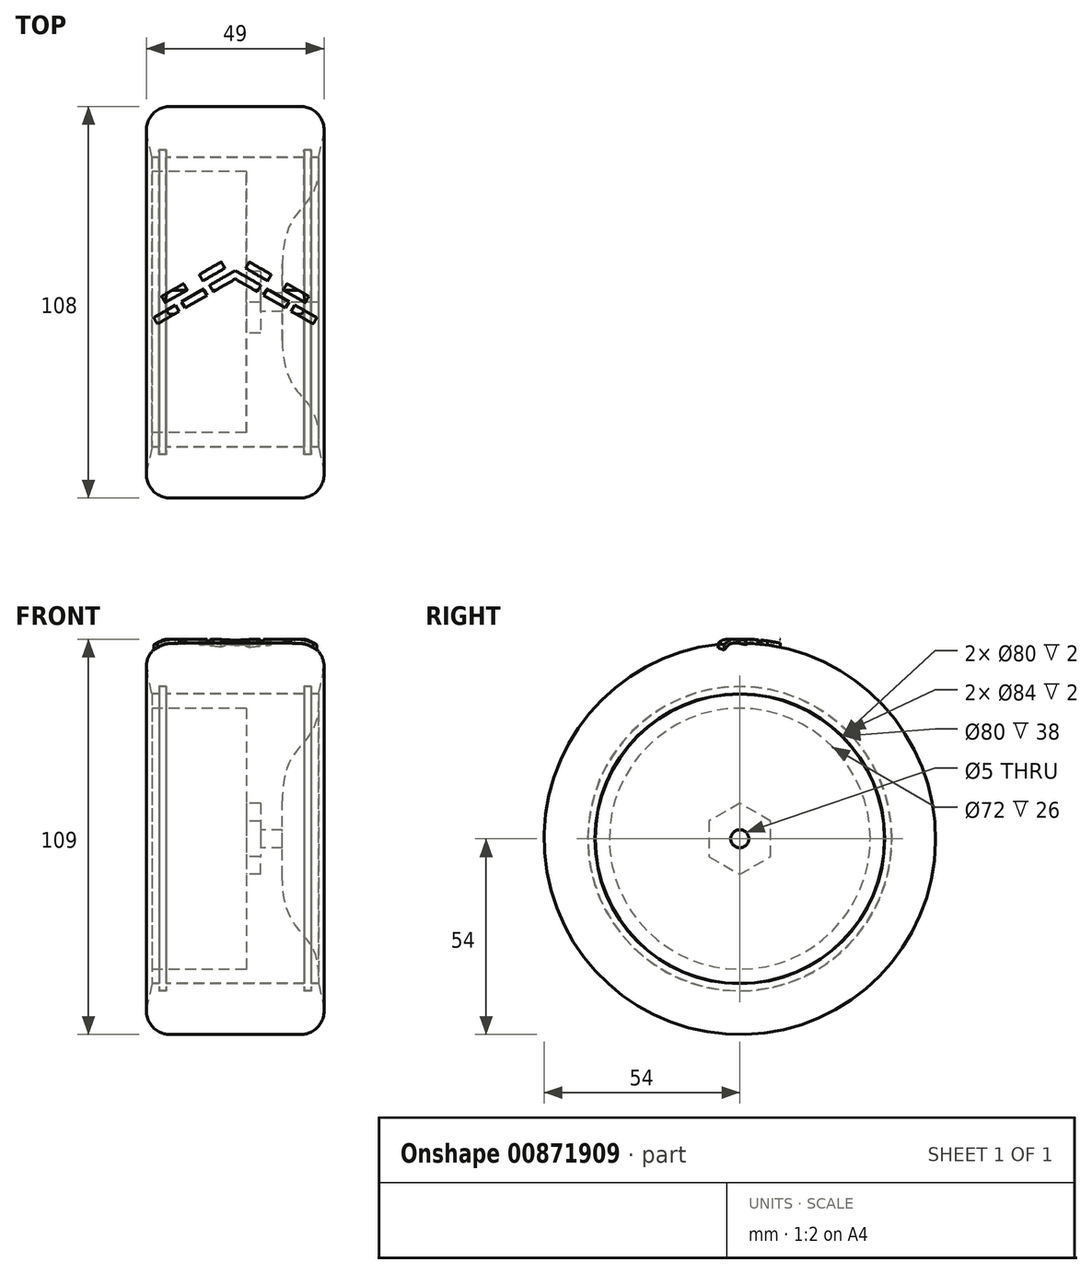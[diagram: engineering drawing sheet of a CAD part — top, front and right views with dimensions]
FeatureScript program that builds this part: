
annotation { "Feature Type Name" : "Feature", "Feature Type Description" : "" }
export const myFeature = defineFeature(function(context is Context, id is Id, definition is map)
    precondition{}
    {
        {
            var Q0;
            Q0=qCreatedBy(makeId("Front.planeOp"),FACE);
            var sketch = newSketch(context, id + "F0", { "sketchPlane" : qUnion([Q0])});
            skLineSegment(sketch, "E0", {"start": v(0, 0) * mm, "end": v(28.5, 0) * mm, "construction": true});
            skLineSegment(sketch, "E1", {"start": v(23, 2.5) * mm, "end": v(3, 2.5) * mm});
            skLineSegment(sketch, "E2", {"start": v(3, 2.5) * mm, "end": v(3, 36) * mm});
            skLineSegment(sketch, "E3", {"start": v(3, 36) * mm, "end": v(-23, 36) * mm});
            skLineSegment(sketch, "E4", {"start": v(-23, 36) * mm, "end": v(-23, 39.9) * mm});
            skLineSegment(sketch, "E5", {"start": v(-15, 54) * mm, "end": v(18, 54) * mm, "construction": true});
            skLineSegment(sketch, "E6", {"start": v(23, 46) * mm, "end": v(23, 40) * mm, "construction": true});
            skLineSegment(sketch, "E7", {"start": v(-23, 40) * mm, "end": v(-21, 40) * mm});
            skLineSegment(sketch, "E8", {"start": v(-21, 40) * mm, "end": v(-21, 42) * mm});
            skLineSegment(sketch, "E9", {"start": v(-21, 42) * mm, "end": v(-19, 42) * mm});
            skLineSegment(sketch, "E10", {"start": v(-19, 42) * mm, "end": v(-19, 40) * mm});
            skLineSegment(sketch, "E11", {"start": v(-19, 40) * mm, "end": v(19, 40) * mm});
            skLineSegment(sketch, "E12", {"start": v(19, 40) * mm, "end": v(19, 42) * mm});
            skLineSegment(sketch, "E13", {"start": v(19, 42) * mm, "end": v(21, 42) * mm});
            skLineSegment(sketch, "E14", {"start": v(21, 42) * mm, "end": v(21, 40) * mm});
            skLineSegment(sketch, "E15", {"start": v(21, 40) * mm, "end": v(23, 40) * mm});
            skLineSegment(sketch, "E16.0", {"start": v(20.9, 39.9) * mm, "end": v(23, 39.9) * mm});
            skLineSegment(sketch, "E16.1", {"start": v(20.9, 41.9) * mm, "end": v(20.9, 39.9) * mm});
            skLineSegment(sketch, "E16.2", {"start": v(19.1, 41.9) * mm, "end": v(20.9, 41.9) * mm});
            skLineSegment(sketch, "E16.3", {"start": v(19.1, 39.9) * mm, "end": v(19.1, 41.9) * mm});
            skLineSegment(sketch, "E16.4", {"start": v(-19.1, 39.9) * mm, "end": v(19.1, 39.9) * mm});
            skLineSegment(sketch, "E16.5", {"start": v(-23, 39.9) * mm, "end": v(-20.9, 39.9) * mm});
            skLineSegment(sketch, "E16.6", {"start": v(-20.9, 39.9) * mm, "end": v(-20.9, 41.9) * mm});
            skLineSegment(sketch, "E16.7", {"start": v(-20.9, 41.9) * mm, "end": v(-19.1, 41.9) * mm});
            skLineSegment(sketch, "E16.8", {"start": v(-19.1, 41.9) * mm, "end": v(-19.1, 39.9) * mm});
            skLineSegment(sketch, "E17.trimOffspring", {"start": v(-23, 40) * mm, "end": v(-23, 46) * mm, "construction": true});
            skLineSegment(sketch, "E18.trimOffspring", {"start": v(23, 39.9) * mm, "end": v(23, 2.5) * mm});
            skPoint(sketch, "E19.visualSharp", {"position": v(-23, 54) * mm});
            skArc(sketch, "E19.filletArc", {"start": v(-15, 54) * mm, "mid": v(-20.66, 51.66) * mm, "end": v(-23, 46) * mm, "construction": true});
            skPoint(sketch, "E20.visualSharp", {"position": v(23, 54) * mm});
            skArc(sketch, "E20.filletArc", {"start": v(23, 46) * mm, "mid": v(20.66, 51.66) * mm, "end": v(15, 54) * mm, "construction": true});
            skLineSegment(sketch, "E21", {"start": v(23, 40) * mm, "end": v(24.35, 46.1) * mm});
            skArc(sketch, "E22", {"start": v(24.35, 46.1) * mm, "mid": v(23.07, 51.57) * mm, "end": v(18, 54) * mm});
            skLineSegment(sketch, "E23", {"start": v(0, 40) * mm, "end": v(0, 59.6) * mm, "construction": true});
            skArc(sketch, "E24.MirrorCS", {"start": v(-24.35, 46.1) * mm, "mid": v(-23.07, 51.57) * mm, "end": v(-18, 54) * mm});
            skLineSegment(sketch, "E25.MirrorCS", {"start": v(-23, 40) * mm, "end": v(-24.35, 46.1) * mm});
            skLineSegment(sketch, "E26", {"start": v(-18, 54) * mm, "end": v(18, 54) * mm});
            skSolve(sketch);
        }
        {
            var Q0;
            Q0=qSketchRegion(id+"F0",true);
            var Q1;
            Q1=sQuery(id+"F0.wireOp",EDGE,"E0");
            revolve(context, id + "F1", {"surfaceOperationType" : NewSurfaceOperationType.NEW, "entities" : qUnion([Q0]), "axis" : qUnion([Q1]), "revolveType" : RevolveType.FULL});
        }
        {
            var Q0;
            Q0=makeQuery(id+"F1.opRevolve","SWEPT_FACE",FACE,{"disambiguationData":[OSD([sQuery(id+"F0.wireOp",EDGE,"E2")])]});
            var sketch = newSketch(context, id + "F2", { "sketchPlane" : qUnion([Q0])});
            skCircle(sketch, "E27.cCircle", {"center": v(0, 0) * mm, "radius": 9.81 * mm, "construction": true});
            skLineSegment(sketch, "E27.0", {"start": v(8.5, 4.9) * mm, "end": v(8.5, -4.9) * mm});
            skLineSegment(sketch, "E27.1", {"start": v(8.5, -4.9) * mm, "end": v(0, -9.81) * mm});
            skLineSegment(sketch, "E27.2", {"start": v(0, -9.81) * mm, "end": v(-8.5, -4.9) * mm});
            skLineSegment(sketch, "E27.3", {"start": v(-8.5, -4.9) * mm, "end": v(-8.5, 4.9) * mm});
            skLineSegment(sketch, "E27.4", {"start": v(-8.5, 4.9) * mm, "end": v(0, 9.81) * mm});
            skLineSegment(sketch, "E27.5", {"start": v(0, 9.81) * mm, "end": v(8.5, 4.9) * mm});
            skSolve(sketch);
        }
        {
            var Q0;
            Q0=qSketchRegion(id+"F2",true);
            extrude(context, id + "F3", {"entities" : qUnion([Q0]), "operationType" : NewBodyOperationType.REMOVE, "oppositeDirection" : true, "depth" : 4 * mm, "offsetDistance" : 25 * mm});
        }
        {
            var Q0;
            Q0=qCreatedBy(makeId("Front.planeOp"),FACE);
            var sketch = newSketch(context, id + "F4", { "sketchPlane" : qUnion([Q0])});
            skLineSegment(sketch, "E28", {"start": v(0, 0) * mm, "end": v(45.35, 0) * mm, "construction": true});
            skLineSegment(sketch, "E29", {"start": v(13, 0) * mm, "end": v(13, 10.5) * mm});
            skLineSegment(sketch, "E30", {"start": v(20.9, 39.9) * mm, "end": v(23, 39.9) * mm, "construction": true});
            skLineSegment(sketch, "E31", {"start": v(23, 39.9) * mm, "end": v(23, 37.9) * mm});
            skFitSpline(sketch, "E32", {"points": [v(23, 37.9) * mm, v(13, 10.5) * mm], "startDerivative": vector(0, -41.43) * mm, "endDerivative": vector(0, -52.48) * mm});
            skLineSegment(sketch, "E33", {"start": v(23, 39.9) * mm, "end": v(24, 39.9) * mm});
            skLineSegment(sketch, "E34", {"start": v(24, 39.9) * mm, "end": v(24, 0) * mm});
            skLineSegment(sketch, "E35", {"start": v(24, 0) * mm, "end": v(13, 0) * mm});
            skSolve(sketch);
        }
        {
            var Q0;
            Q0=makeQuery(id+"F4.imprint","IMPRINT",FACE,{"disambiguationData":[TD([[makeQuery(id+"F4.imprint","IMPRINT",EDGE,{"derivedFrom":sQuery(id+"F4.wireOp",EDGE,"E29")}),-1.0]])]});
            var Q1;
            Q1=sQuery(id+"F4.wireOp",EDGE,"E28");
            revolve(context, id + "F5", {"operationType" : NewBodyOperationType.REMOVE, "surfaceOperationType" : NewSurfaceOperationType.NEW, "entities" : qUnion([Q0]), "axis" : qUnion([Q1]), "revolveType" : RevolveType.FULL, "oppositeDirection" : true});
        }
        {
            var Q0;
            Q0=qCreatedBy(makeId("Top.planeOp"),FACE);
            cPlane(context, id + "F6", {"entities" : qUnion([Q0]), "cplaneType" : CPlaneType.OFFSET, "offset" : (110 / 2) * mm, "width" : 150 * mm, "height" : 150 * mm});
        }
        {
            var Q0;
            Q0=qCreatedBy(id+"F6.planeOp",FACE);
            var sketch = newSketch(context, id + "F7", { "sketchPlane" : qUnion([Q0])});
            skLineSegment(sketch, "E36", {"start": v(-24.5, -48.5) * mm, "end": v(-24.5, 48.5) * mm, "construction": true});
            skLineSegment(sketch, "E37", {"start": v(24.5, -48.5) * mm, "end": v(24.5, 48.5) * mm, "construction": true});
            skLineSegment(sketch, "E38", {"start": v(-24.5, 0) * mm, "end": v(24.5, 0) * mm, "construction": true});
            skLineSegment(sketch, "E39", {"start": v(-21.5, -6) * mm, "end": v(0, 6.41) * mm, "construction": true});
            skLineSegment(sketch, "E40", {"start": v(0, 6.41) * mm, "end": v(21.5, -6) * mm, "construction": true});
            skLineSegment(sketch, "E41", {"start": v(21.5, -6) * mm, "end": v(22.5, -4.27) * mm});
            skLineSegment(sketch, "E42", {"start": v(22.5, -4.27) * mm, "end": v(0, 8.72) * mm, "construction": true});
            skLineSegment(sketch, "E43", {"start": v(0, 8.72) * mm, "end": v(-22.5, -4.27) * mm, "construction": true});
            skLineSegment(sketch, "E44", {"start": v(-22.5, -4.27) * mm, "end": v(-21.5, -6) * mm});
            skLineSegment(sketch, "E45", {"start": v(0, 0) * mm, "end": v(0, 13.9) * mm, "construction": true});
            skLineSegment(sketch, "E46", {"start": v(-21.5, -6) * mm, "end": v(21.5, -6) * mm, "construction": true});
            skLineSegment(sketch, "E47", {"start": v(0, 0) * mm, "end": v(0, -10.86) * mm, "construction": true});
            skLineSegment(sketch, "E48", {"start": v(21.5, -6) * mm, "end": v(15.44, -2.5) * mm});
            skLineSegment(sketch, "E49", {"start": v(15.44, -2.5) * mm, "end": v(16.44, -0.77) * mm});
            skLineSegment(sketch, "E50", {"start": v(16.44, -0.77) * mm, "end": v(22.5, -4.27) * mm});
            skLineSegment(sketch, "E51", {"start": v(-21.5, -6) * mm, "end": v(-15.44, -2.5) * mm});
            skLineSegment(sketch, "E52", {"start": v(-15.44, -2.5) * mm, "end": v(-16.44, -0.77) * mm});
            skLineSegment(sketch, "E53", {"start": v(-16.44, -0.77) * mm, "end": v(-22.5, -4.27) * mm});
            skLineSegment(sketch, "E54", {"start": v(-14.86, 0.15) * mm, "end": v(-13.86, -1.59) * mm});
            skLineSegment(sketch, "E55", {"start": v(-13.86, -1.59) * mm, "end": v(-7.8, 1.91) * mm});
            skLineSegment(sketch, "E56", {"start": v(-7.8, 1.91) * mm, "end": v(-8.8, 3.65) * mm});
            skLineSegment(sketch, "E57", {"start": v(-8.8, 3.65) * mm, "end": v(-14.86, 0.15) * mm});
            skLineSegment(sketch, "E58", {"start": v(8.8, 3.65) * mm, "end": v(7.8, 1.91) * mm});
            skLineSegment(sketch, "E59", {"start": v(7.8, 1.91) * mm, "end": v(13.86, -1.59) * mm});
            skLineSegment(sketch, "E60", {"start": v(13.86, -1.59) * mm, "end": v(14.86, 0.15) * mm});
            skLineSegment(sketch, "E61", {"start": v(14.86, 0.15) * mm, "end": v(8.8, 3.65) * mm});
            skLineSegment(sketch, "E62", {"start": v(7.06, 4.65) * mm, "end": v(6.06, 2.91) * mm});
            skLineSegment(sketch, "E63", {"start": v(6.06, 2.91) * mm, "end": v(0, 6.41) * mm});
            skLineSegment(sketch, "E64", {"start": v(-6.06, 2.91) * mm, "end": v(-7.06, 4.65) * mm});
            skLineSegment(sketch, "E65", {"start": v(-7.06, 4.65) * mm, "end": v(0, 8.72) * mm});
            skLineSegment(sketch, "E66", {"start": v(7.06, 4.65) * mm, "end": v(0, 8.72) * mm});
            skLineSegment(sketch, "E67", {"start": v(-6.06, 2.91) * mm, "end": v(0, 6.41) * mm});
            skLineSegment(sketch, "E68.0", {"start": v(0, 11.03) * mm, "end": v(-23.5, -2.54) * mm, "construction": true});
            skLineSegment(sketch, "E68.1", {"start": v(23.5, -2.54) * mm, "end": v(0, 11.03) * mm, "construction": true});
            skLineSegment(sketch, "E69.0", {"start": v(-1, 12.76) * mm, "end": v(-24.5, -0.8) * mm, "construction": true});
            skLineSegment(sketch, "E70", {"start": v(-20.32, 1.6) * mm, "end": v(-19.32, -0.12) * mm});
            skLineSegment(sketch, "E71", {"start": v(-19.32, -0.12) * mm, "end": v(-13.26, 3.38) * mm});
            skLineSegment(sketch, "E72", {"start": v(-13.26, 3.38) * mm, "end": v(-14.26, 5.1) * mm});
            skLineSegment(sketch, "E73", {"start": v(-14.26, 5.1) * mm, "end": v(-20.32, 1.6) * mm});
            skLineSegment(sketch, "E74", {"start": v(-8.93, 5.88) * mm, "end": v(-9.93, 7.6) * mm});
            skLineSegment(sketch, "E75", {"start": v(-9.93, 7.6) * mm, "end": v(-3.87, 11.1) * mm});
            skLineSegment(sketch, "E76", {"start": v(-3.87, 11.1) * mm, "end": v(-2.87, 9.38) * mm});
            skLineSegment(sketch, "E77", {"start": v(-2.87, 9.38) * mm, "end": v(-8.93, 5.88) * mm});
            skLineSegment(sketch, "E78.MirrorCS", {"start": v(3.87, 11.1) * mm, "end": v(2.87, 9.38) * mm});
            skLineSegment(sketch, "E79.MirrorCS", {"start": v(8.93, 5.88) * mm, "end": v(9.93, 7.6) * mm});
            skLineSegment(sketch, "E80.MirrorCS", {"start": v(13.26, 3.38) * mm, "end": v(14.26, 5.1) * mm});
            skLineSegment(sketch, "E81.MirrorCS", {"start": v(20.32, 1.6) * mm, "end": v(19.32, -0.12) * mm});
            skLineSegment(sketch, "E82", {"start": v(2.87, 9.38) * mm, "end": v(8.93, 5.88) * mm});
            skLineSegment(sketch, "E83", {"start": v(9.93, 7.6) * mm, "end": v(3.87, 11.1) * mm});
            skLineSegment(sketch, "E84", {"start": v(14.26, 5.1) * mm, "end": v(20.32, 1.6) * mm});
            skLineSegment(sketch, "E85", {"start": v(19.32, -0.12) * mm, "end": v(13.26, 3.38) * mm});
            skSolve(sketch);
        }
        {
            var Q0;
            Q0=qSketchRegion(id+"F7",true);
            extrude(context, id + "F8", {"entities" : qUnion([Q0]), "operationType" : NewBodyOperationType.ADD, "oppositeDirection" : true, "depth" : 5 * mm, "offsetDistance" : 25 * mm});
        }
        {
            var Q0;
            Q0=qCreatedBy(makeId("Front.planeOp"),FACE);
            var sketch = newSketch(context, id + "F9", { "sketchPlane" : qUnion([Q0])});
            skArc(sketch, "E86", {"start": v(-24.35, -46.1) * mm, "mid": v(-24.46, -46.8) * mm, "end": v(-24.5, -47.5) * mm, "construction": true});
            skArc(sketch, "E87", {"start": v(-24.5, 47.5) * mm, "mid": v(-24.46, 46.8) * mm, "end": v(-24.35, 46.1) * mm, "construction": true});
            skArc(sketch, "E88", {"start": v(-24.35, -46.1) * mm, "mid": v(-24.46, -46.8) * mm, "end": v(-24.5, -47.5) * mm});
            skArc(sketch, "E89", {"start": v(-24.5, 47.5) * mm, "mid": v(-24.46, 46.8) * mm, "end": v(-24.35, 46.1) * mm});
            skLineSegment(sketch, "E90", {"start": v(-45.98, 54) * mm, "end": v(37.08, 54) * mm, "construction": true});
            skCircle(sketch, "E91", {"center": v(-18, 47.5) * mm, "radius": 6.5 * mm, "construction": true});
            skArc(sketch, "E92", {"start": v(-18, 55.1) * mm, "mid": v(-23.37, 52.87) * mm, "end": v(-25.6, 47.5) * mm});
            skLineSegment(sketch, "E93", {"start": v(-25.6, 47.5) * mm, "end": v(-29, 47.5) * mm});
            skLineSegment(sketch, "E94", {"start": v(-29, 47.5) * mm, "end": v(-29, 56.1) * mm});
            skArc(sketch, "E95", {"start": v(24.35, 46.1) * mm, "mid": v(24.46, 46.8) * mm, "end": v(24.5, 47.5) * mm, "construction": true});
            skArc(sketch, "E96", {"start": v(25.6, 47.5) * mm, "mid": v(23.37, 52.87) * mm, "end": v(18, 55.1) * mm});
            skLineSegment(sketch, "E97.trimOffspring", {"start": v(-18, 55.1) * mm, "end": v(18, 55.1) * mm});
            skLineSegment(sketch, "E98", {"start": v(25.6, 47.5) * mm, "end": v(29, 47.5) * mm});
            skLineSegment(sketch, "E99", {"start": v(29, 47.5) * mm, "end": v(29, 56.1) * mm});
            skLineSegment(sketch, "E100", {"start": v(29, 56.1) * mm, "end": v(-29, 56.1) * mm});
            skLineSegment(sketch, "E101", {"start": v(0, 0) * mm, "end": v(60.16, 0) * mm, "construction": true});
            skSolve(sketch);
        }
        {
            var Q0;
            Q0=makeQuery(id+"F9.imprint","IMPRINT",FACE,{"disambiguationData":[TD([[makeQuery(id+"F9.imprint","IMPRINT",EDGE,{"derivedFrom":sQuery(id+"F9.wireOp",EDGE,"E92")}),-1.0]])]});
            var Q1;
            Q1=qConstructionFilter(qBodyType(qCreatedBy(id+"F9",EDGE),BodyType.WIRE),ConstructionObject.NO);
            var Q2;
            Q2=sQuery(id+"F9.wireOp",EDGE,"E101");
            revolve(context, id + "F10", {"operationType" : NewBodyOperationType.REMOVE, "surfaceOperationType" : NewSurfaceOperationType.NEW, "entities" : qUnion([Q0]), "surfaceEntities" : qUnion([Q1]), "axis" : qUnion([Q2]), "revolveType" : RevolveType.FULL, "oppositeDirection" : true});
        }
    });
